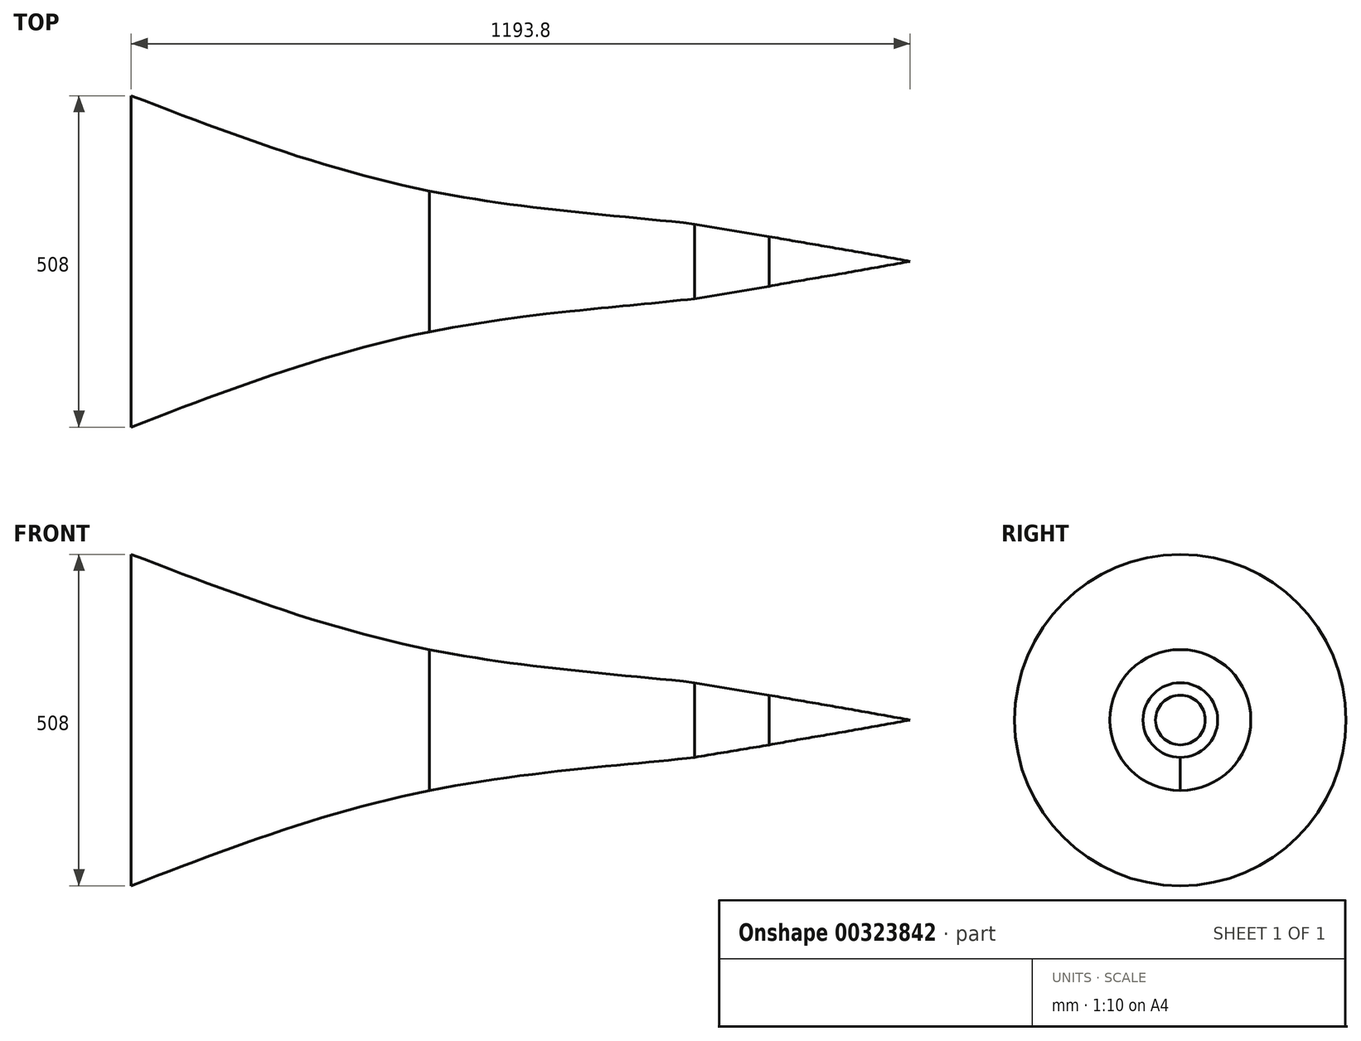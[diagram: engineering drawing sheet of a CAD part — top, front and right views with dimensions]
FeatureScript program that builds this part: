
annotation { "Feature Type Name" : "Feature", "Feature Type Description" : "" }
export const myFeature = defineFeature(function(context is Context, id is Id, definition is map)
    precondition{}
    {
        {
            var Q0;
            Q0=qCreatedBy(makeId("Top.planeOp"),FACE);
            var sketch = newSketch(context, id + "F0", { "sketchPlane" : qUnion([Q0])});
            skLineSegment(sketch, "E0", {"start": v(0, 0) * mm, "end": v(-114.3, 0) * mm});
            skLineSegment(sketch, "E1", {"start": v(-114.3, 0) * mm, "end": v(-215.9, 0) * mm});
            skLineSegment(sketch, "E2", {"start": v(-215.9, 0) * mm, "end": v(-330.2, 0) * mm});
            skLineSegment(sketch, "E3", {"start": v(-330.2, 0) * mm, "end": v(-1193.8, 0) * mm});
            skLineSegment(sketch, "E4", {"start": v(-736.6, 0) * mm, "end": v(-1193.8, 0) * mm});
            skLineSegment(sketch, "E5", {"start": v(-114.3, 0) * mm, "end": v(-114.3, -20.32) * mm});
            skLineSegment(sketch, "E6", {"start": v(-215.9, 0) * mm, "end": v(-215.9, -38.1) * mm});
            skLineSegment(sketch, "E7", {"start": v(-330.2, 0) * mm, "end": v(-330.2, -57.15) * mm});
            skLineSegment(sketch, "E8", {"start": v(-736.6, 0) * mm, "end": v(-736.6, -107.95) * mm});
            skLineSegment(sketch, "E9", {"start": v(-1193.8, 0) * mm, "end": v(-1193.8, -254) * mm});
            skLineSegment(sketch, "E10", {"start": v(-215.9, -38.1) * mm, "end": v(-330.2, -57.15) * mm});
            skLineSegment(sketch, "E11", {"start": v(-114.3, -20.32) * mm, "end": v(-215.9, -38.1) * mm});
            skLineSegment(sketch, "E12", {"start": v(-330.2, -57.15) * mm, "end": v(-736.6, -107.95) * mm});
            skFitSpline(sketch, "E13.trimOffspring", {"points": [v(0, 0) * mm, v(-114.3, -20.32) * mm, v(-215.9, -38.1) * mm, v(-330.2, -57.15) * mm, v(-736.6, -107.95) * mm, v(-1193.8, -254) * mm], "startDerivative": vector(-789.71, -142.35) * mm, "endDerivative": vector(-1491.14, -573.97) * mm});
            skLineSegment(sketch, "E14", {"start": v(0, 0) * mm, "end": v(0, -17.78) * mm});
            skLineSegment(sketch, "E15", {"start": v(0, -17.78) * mm, "end": v(-114.3, -20.32) * mm});
            skSolve(sketch);
        }
        {
            var Q0;
            Q0=makeQuery(id+"F0.imprint","IMPRINT",FACE,{"disambiguationData":[TD([[makeQuery(id+"F0.imprint","IMPRINT",EDGE,{"derivedFrom":sQuery(id+"F0.wireOp",EDGE,"E4")}),1.0]])]});
            var Q1;
            Q1=makeQuery(id+"F0.imprint","IMPRINT",FACE,{"disambiguationData":[TD([[makeQuery(id+"F0.imprint","IMPRINT",EDGE,{"derivedFrom":sQuery(id+"F0.wireOp",EDGE,"E3")}),1.0]])]});
            var Q2;
            Q2=makeQuery(id+"F0.imprint","IMPRINT",FACE,{"disambiguationData":[TD([[makeQuery(id+"F0.imprint","IMPRINT",EDGE,{"derivedFrom":sQuery(id+"F0.wireOp",EDGE,"E2")}),1.0]])]});
            var Q3;
            Q3=makeQuery(id+"F0.imprint","IMPRINT",FACE,{"disambiguationData":[TD([[makeQuery(id+"F0.imprint","IMPRINT",EDGE,{"derivedFrom":sQuery(id+"F0.wireOp",EDGE,"E1")}),1.0]])]});
            var Q4;
            Q4=makeQuery(id+"F0.imprint","IMPRINT",FACE,{"disambiguationData":[TD([[makeQuery(id+"F0.imprint","IMPRINT",EDGE,{"derivedFrom":sQuery(id+"F0.wireOp",EDGE,"E0")}),1.0]])]});
            var Q5;
            Q5=sQuery(id+"F0.wireOp",EDGE,"E4");
            revolve(context, id + "F1", {"surfaceOperationType" : NewSurfaceOperationType.NEW, "entities" : qUnion([Q0, Q1, Q2, Q3, Q4]), "axis" : qUnion([Q5]), "revolveType" : RevolveType.FULL});
        }
    });
